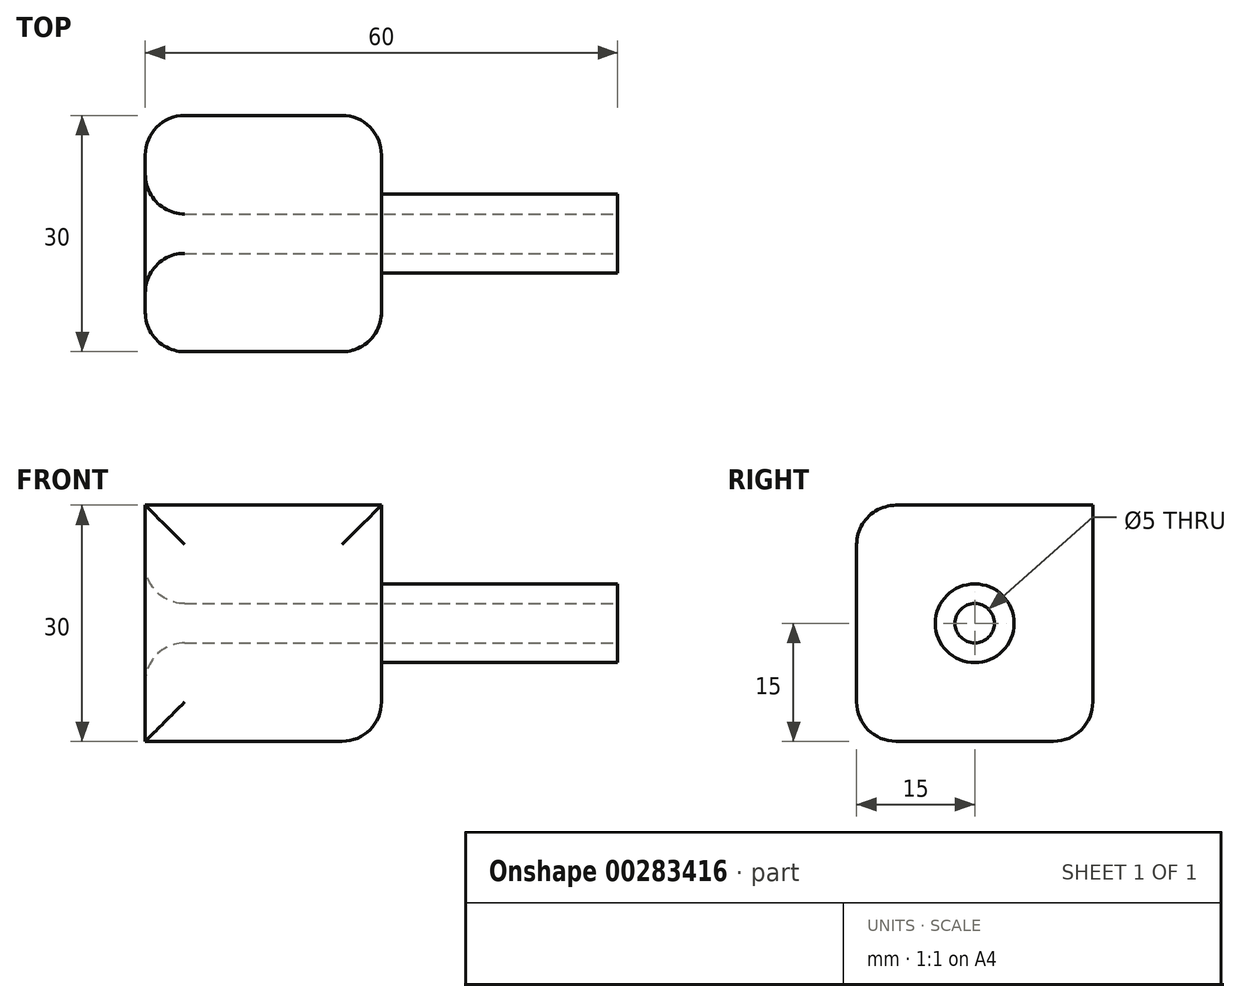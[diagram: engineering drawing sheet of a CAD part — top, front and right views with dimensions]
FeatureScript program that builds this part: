
annotation { "Feature Type Name" : "Feature", "Feature Type Description" : "" }
export const myFeature = defineFeature(function(context is Context, id is Id, definition is map)
    precondition{}
    {
        {
            var Q0;
            Q0=qCreatedBy(makeId("Right.planeOp"),FACE);
            var sketch = newSketch(context, id + "F0", { "sketchPlane" : qUnion([Q0])});
            skLineSegment(sketch, "E0.bottom", {"start": v(15, 15) * mm, "end": v(-15, 15) * mm});
            skLineSegment(sketch, "E0.top", {"start": v(15, -15) * mm, "end": v(-15, -15) * mm});
            skLineSegment(sketch, "E0.left", {"start": v(15, 15) * mm, "end": v(15, -15) * mm});
            skLineSegment(sketch, "E0.right", {"start": v(-15, 15) * mm, "end": v(-15, -15) * mm});
            skPoint(sketch, "E0.middle", {"position": v(0, 0) * mm});
            skSolve(sketch);
        }
        {
            var Q0;
            Q0 = qSketchRegion(id + "F0", true);
            extrude(context, id + "F1", {"entities" : qUnion([Q0]), "depth" : 30 * mm});
        }
        {
            var Q0;
            Q0=makeQuery(id+"F1.opExtrude","CAP_FACE",FACE,{"disambiguationData":[OSD([sQuery(id+"F0.wireOp",EDGE,"E0.bottom"),sQuery(id+"F0.wireOp",EDGE,"E0.top"),sQuery(id+"F0.wireOp",EDGE,"E0.left"),sQuery(id+"F0.wireOp",EDGE,"E0.right")])],"isStart":false});
            var sketch = newSketch(context, id + "F2", { "sketchPlane" : qUnion([Q0])});
            skCircle(sketch, "E1", {"center": v(0, 0) * mm, "radius": 5 * mm});
            skSolve(sketch);
        }
        {
            var Q0;
            Q0 = qSketchRegion(id + "F2", true);
            extrude(context, id + "F3", {"entities" : qUnion([Q0]), "operationType" : NewBodyOperationType.ADD, "depth" : 30 * mm});
        }
        {
            var Q0;
            Q0=makeQuery(id+"F3.opExtrude","CAP_FACE",FACE,{"disambiguationData":[OSD([sQuery(id+"F2.wireOp",EDGE,"E1")])],"isStart":false});
            var sketch = newSketch(context, id + "F4", { "sketchPlane" : qUnion([Q0])});
            skCircle(sketch, "E2", {"center": v(0, 0) * mm, "radius": 2.5 * mm});
            skSolve(sketch);
        }
        {
            var Q0;
            Q0=makeQuery(id+"F4.imprint","IMPRINT",FACE,{"disambiguationData":[TD([[makeQuery(id+"F4.imprint","IMPRINT",EDGE,{"derivedFrom":sQuery(id+"F4.wireOp",EDGE,"E2")}),1.0]])]});
            var Q1;
            Q1=sQuery(id+"F4.wireOp",EDGE,"E2");
            extrude(context, id + "F5", {"entities" : qUnion([Q0]), "operationType" : NewBodyOperationType.REMOVE, "surfaceEntities" : qUnion([Q1]), "endBound" : BoundingType.THROUGH_ALL, "oppositeDirection" : true, "depth" : 25 * mm});
        }
        {
            var Q0;
            Q0=makeQuery(id+"F3.opExtrude","CAP_EDGE",EDGE,{"disambiguationData":[OSD([sQuery(id+"F2.wireOp",EDGE,"E1")])],"isStart":true});
            var Q1;
            Q1=makeQuery(id+"F1.opExtrude","CAP_EDGE",EDGE,{"disambiguationData":[OSD([sQuery(id+"F0.wireOp",EDGE,"E0.top")])],"isStart":false});
            var Q2;
            Q2=makeQuery(id+"F1.opExtrude","SWEPT_EDGE",EDGE,{"disambiguationData":[OSD([sQuery(id+"F0.wireOp",EDGE,"E0.top"),sQuery(id+"F0.wireOp",EDGE,"E0.left")])]});
            var Q3;
            Q3=makeQuery(id+"F1.opExtrude","SWEPT_FACE",FACE,{"disambiguationData":[OSD([sQuery(id+"F0.wireOp",EDGE,"E0.right")])]});
            var Q4;
            Q4=makeQuery(id+"F1.opExtrude","CAP_EDGE",EDGE,{"disambiguationData":[OSD([sQuery(id+"F0.wireOp",EDGE,"E0.left")])],"isStart":true});
            var Q5;
            Q5=makeQuery(id+"F1.opExtrude","CAP_EDGE",EDGE,{"disambiguationData":[OSD([sQuery(id+"F0.wireOp",EDGE,"E0.left")])],"isStart":false});
            var Q6;
            Q6=makeQuery(id+"F5.boolean.opBoolean","INTERSECT",EDGE,{"derivedFrom":[makeQuery(id+"F1.opExtrude","CAP_FACE",FACE,{"disambiguationData":[OSD([sQuery(id+"F0.wireOp",EDGE,"E0.bottom"),sQuery(id+"F0.wireOp",EDGE,"E0.top"),sQuery(id+"F0.wireOp",EDGE,"E0.left"),sQuery(id+"F0.wireOp",EDGE,"E0.right")])],"isStart":true}),makeQuery(id+"F5.opExtrude","SWEPT_FACE",FACE,{"disambiguationData":[OSD([sQuery(id+"F4.wireOp",EDGE,"E2")])]})]});
            var Q7;
            Q7=makeQuery(id+"F5.boolean.opBoolean","COPY",EDGE,{"derivedFrom":makeQuery(id+"F5.opExtrude","CAP_EDGE",EDGE,{"disambiguationData":[OSD([sQuery(id+"F4.wireOp",EDGE,"E2")])],"isStart":true})});
            fillet(context, id + "F6", {"entities" : qUnion([Q0, Q1, Q2, Q3, Q4, Q5, Q6, Q7]), "radius" : 5 * mm, "tangentPropagation" : true, "allowEdgeOverflow" : false});
        }
    });
